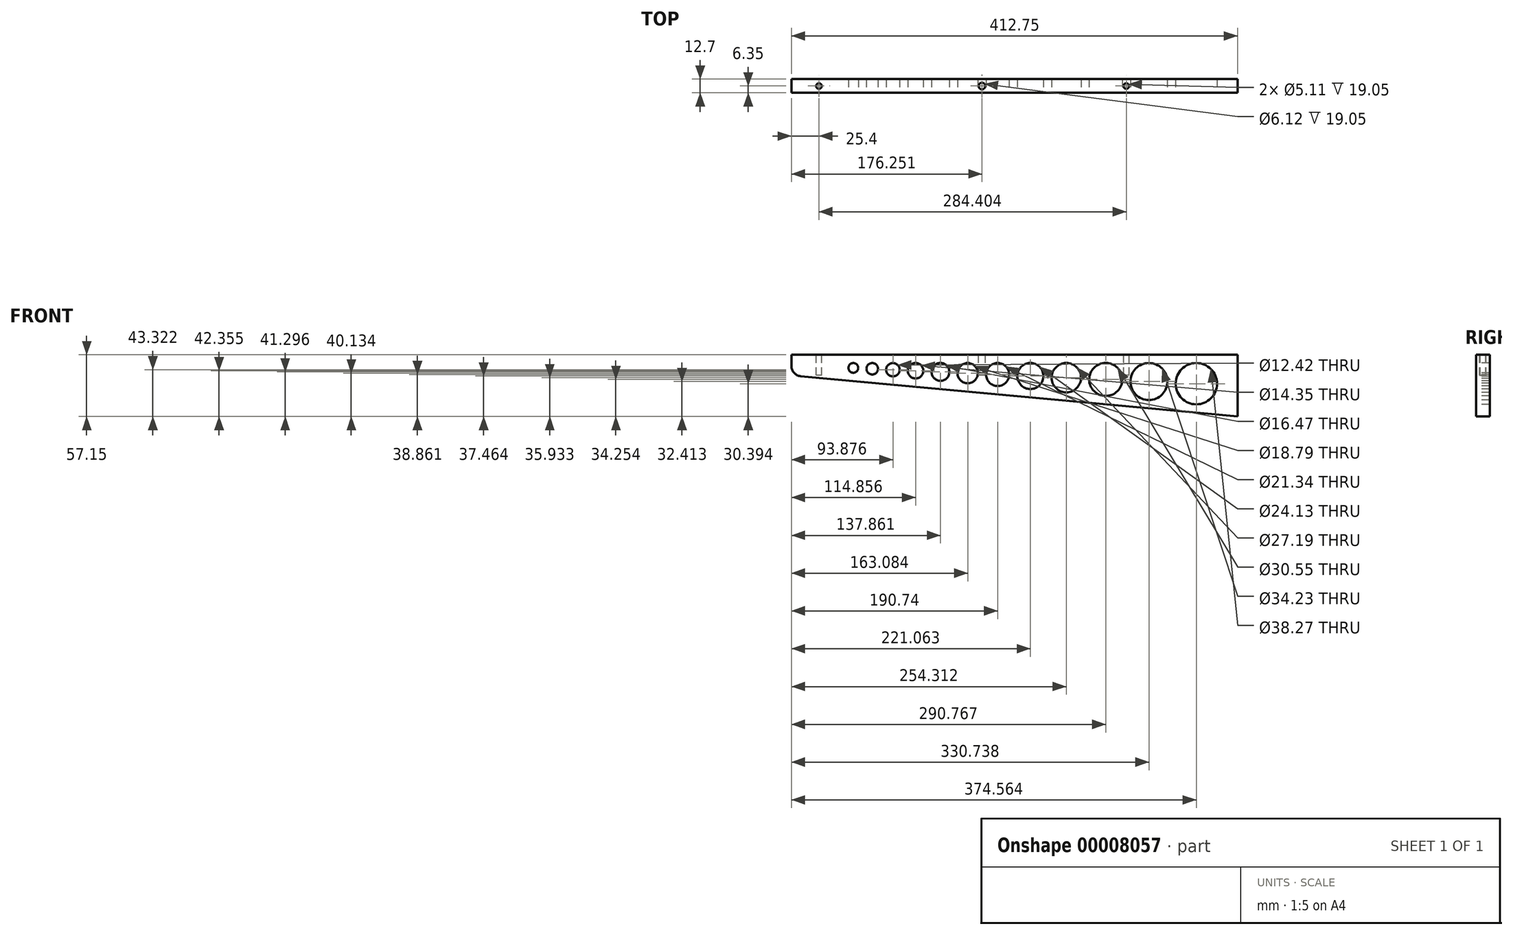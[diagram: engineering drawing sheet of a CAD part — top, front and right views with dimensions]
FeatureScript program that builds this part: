
annotation { "Feature Type Name" : "Feature", "Feature Type Description" : "" }
export const myFeature = defineFeature(function(context is Context, id is Id, definition is map)
    precondition{}
    {
        {
            var Q0;
            Q0=qCreatedBy(makeId("Front.planeOp"),FACE);
            var sketch = newSketch(context, id + "F0", { "sketchPlane" : qUnion([Q0])});
            skLineSegment(sketch, "E0", {"start": v(0, 0) * mm, "end": v(-412.75, 0) * mm});
            skLineSegment(sketch, "E1", {"start": v(-412.75, 0) * mm, "end": v(-412.75, -10.36) * mm});
            skLineSegment(sketch, "E2", {"start": v(-404.1, -19.85) * mm, "end": v(0, -57.15) * mm});
            skLineSegment(sketch, "E3", {"start": v(0, -57.15) * mm, "end": v(0, 0) * mm});
            skPoint(sketch, "E4.visualSharp", {"position": v(-412.75, -19.05) * mm});
            skArc(sketch, "E4.filletArc", {"start": v(-412.75, -10.36) * mm, "mid": v(-410.26, -16.78) * mm, "end": v(-404.1, -19.85) * mm});
            skSolve(sketch);
        }
        {
            var Q0;
            Q0=makeQuery(id+"F0.imprint","IMPRINT",FACE,{"disambiguationData":[TD([[makeQuery(id+"F0.imprint","IMPRINT",EDGE,{"derivedFrom":sQuery(id+"F0.wireOp",EDGE,"E0")}),1.0]])]});
            extrude(context, id + "F1", {"entities" : qUnion([Q0]), "depth" : 12.7 * mm});
        }
        {
            var Q0;
            Q0=makeQuery(id+"F1.opExtrude","CAP_FACE",FACE,{"disambiguationData":[OSD([sQuery(id+"F0.wireOp",EDGE,"E0"),sQuery(id+"F0.wireOp",EDGE,"E1"),sQuery(id+"F0.wireOp",EDGE,"E2"),sQuery(id+"F0.wireOp",EDGE,"E3"),sQuery(id+"F0.wireOp",EDGE,"E4.filletArc")])],"isStart":false});
            var sketch = newSketch(context, id + "F2", { "sketchPlane" : qUnion([Q0])});
            skLineSegment(sketch, "E5", {"start": v(0, 0) * mm, "end": v(0, -7.62) * mm, "construction": true});
            skLineSegment(sketch, "E6", {"start": v(0, -7.62) * mm, "end": v(-453.67, -7.62) * mm, "construction": true});
            skLineSegment(sketch, "E7", {"start": v(0, -57.15) * mm, "end": v(0.7, -49.56) * mm, "construction": true});
            skLineSegment(sketch, "E8", {"start": v(0.7, -49.56) * mm, "end": v(-453.67, -7.62) * mm, "construction": true});
            skCircle(sketch, "E9", {"center": v(-38.19, -26.76) * mm, "radius": 19.14 * mm});
            skCircle(sketch, "E10", {"center": v(-82.01, -24.74) * mm, "radius": 17.12 * mm});
            skCircle(sketch, "E11", {"center": v(-121.98, -22.9) * mm, "radius": 15.28 * mm});
            skCircle(sketch, "E12", {"center": v(-158.44, -21.22) * mm, "radius": 13.6 * mm});
            skCircle(sketch, "E13", {"center": v(-191.69, -19.69) * mm, "radius": 12.07 * mm});
            skCircle(sketch, "E14", {"center": v(-222.01, -18.29) * mm, "radius": 10.67 * mm});
            skCircle(sketch, "E15", {"center": v(-249.67, -17.02) * mm, "radius": 9.4 * mm});
            skCircle(sketch, "E16", {"center": v(-274.89, -15.85) * mm, "radius": 8.23 * mm});
            skCircle(sketch, "E17", {"center": v(-297.9, -14.8) * mm, "radius": 7.17 * mm});
            skCircle(sketch, "E18", {"center": v(-318.87, -13.83) * mm, "radius": 6.2 * mm});
            skCircle(sketch, "E19", {"center": v(-338, -12.95) * mm, "radius": 5.33 * mm});
            skCircle(sketch, "E20", {"center": v(-355.46, -12.14) * mm, "radius": 4.52 * mm});
            skSolve(sketch);
        }
        {
            var Q0;
            Q0 = qSketchRegion(id + "F2", true);
            extrude(context, id + "F3", {"entities" : qUnion([Q0]), "operationType" : NewBodyOperationType.REMOVE, "endBound" : BoundingType.THROUGH_ALL, "oppositeDirection" : true, "depth" : 25.4 * mm});
        }
        {
            var Q0;
            Q0=makeQuery(id+"F1.opExtrude","SWEPT_FACE",FACE,{"disambiguationData":[OSD([sQuery(id+"F0.wireOp",EDGE,"E0")])]});
            var sketch = newSketch(context, id + "F4", { "sketchPlane" : qUnion([Q0])});
            skCircle(sketch, "E21", {"center": v(-102.95, -6.35) * mm, "radius": 2.55 * mm});
            skCircle(sketch, "E22", {"center": v(-387.35, -6.35) * mm, "radius": 2.55 * mm});
            skCircle(sketch, "E23", {"center": v(-583.39, -6.35) * mm, "radius": 5.53 * mm});
            skCircle(sketch, "E24", {"center": v(-236.5, -6.35) * mm, "radius": 3.06 * mm});
            skSolve(sketch);
        }
        {
            var Q0;
            Q0 = qSketchRegion(id + "F4", true);
            var Q1;
            Q1=sQuery(id+"F4.wireOp",EDGE,"E22");
            var Q2;
            Q2=sQuery(id+"F4.wireOp",EDGE,"E24");
            var Q3;
            Q3=sQuery(id+"F4.wireOp",EDGE,"E21");
            extrude(context, id + "F5", {"entities" : qUnion([Q0]), "operationType" : NewBodyOperationType.REMOVE, "surfaceEntities" : qUnion([Q1, Q2, Q3]), "oppositeDirection" : true, "depth" : 19.05 * mm});
        }
    });
